# Revit family: 30501
name_source: partatom
category: Lighting Fixtures
revit_build: Autodesk Revit 2018 (Build: 20170223_1515(x64)
units: mm (PartAtom-declared; Revit-internal decimal feet)

## family parameters
Cut with Voids When Loaded = No
Host = Face
Light Source = Yes
OmniClass Number = 23.80.70.00
OmniClass Title = Lighting
Part Type = Normal
Room Calculation Point = No
Round Connector Dimension = Use Diameter
Shared = No

## types (1)
- 0030501 INSAVER SLIM UGR19 IP44 150 1200LM 840
    Apparent Load = 10 VA
    Assembly Code = D5020200
    AssetType = Fixed
    ClassificationName = Uniclass2015
    ClassificationValue = EF_70_80
    Color Filter = 16777215
    Cost = 0 $
    Default Elevation = 1219 mm
    Description = Insaver Slim is a ceiling recessed LED downlight (IP44 from the front),Die-cast aluminium body, loop in loop out connector for quick installation, Non dimmable LED driver, 9.5W; 1200lm; 126lm/W; 4000K; UGR <19 with shallow product depth 50mm. Meets TP(a) requirements.
    DiameterRecess_SYL = 150 mm
    DiameterTopBase_SYL = 150 mm
    DiameterTop_SYL = 98 mm  [stored 0.321522 ft]
    Diameter_SYL = 165 mm
    Dimming Lamp Color Temperature Shift = <None>
    DocumentationLiterature = http://www.sylvania-lighting.com
    DurationUnit = hours
    ElectricShockClassification = 126
    Emit Shape Visible in Rendering = No
    Emit from Circle Diameter = 125 mm  [stored 0.410105 ft]
    ExpectedLife = 50000
    HeightBezel_SYL = 3 mm  [stored 0.00984252 ft]
    Height_SYL = 61 mm  [stored 0.200131 ft]
    IfcExportAs = Class II
    IfcExportType = IfcLightFixtureType
    ImpactProtectionIndex = IfcLightFixtureType
    IngressProtection = IfcLightFixtureType
    InputNominalFrequency = 4000
    InputVoltage = 0
    LampColourRenderingIndex = 16500
    LampColourTemperature = LED
    LampMacAdamStep = 80
    LampNominalLuminous = 4000 K
    LightOutputRatio = LED
    LuminaireType = 0
    ManufacturerName = 126 lm/W
    Material = Feilo Sylvania
    Material_1_FEILO = Trim-Sylvania-STARTDownlight-White
    Material_2_FEILO = Diffuser-Sylvania-STARTDownlight
    Material_3_FEILO = Top-Sylvania-STARTDownlight
    Material_4_FEILO = LED-Sylvania-STARTDownlight
    Model = Insaver Slim UGR19 IP44 150 1200lm 840
    ModelNumber = 0030501
    ModelReference = Insaver Slim UGR19 IP44 150 1200lm 840
    Name = Insaver Slim UGR19 IP44 150 1200lm 840
    NominalDepth = 165 mm
    NominalHeight = 50 mm  [stored 0.164042 ft]
    NominalLength = 165 mm
    Photometric Web File = 0030501.IES
    PowerConsumption = Lighting
    PowerFactor = 0.9
    RadiusReflector_SYL = 85 mm  [stored 0.278871 ft]
    RadiusTop_SYL = 6 mm  [stored 0.019685 ft]
    Size1_SYL = Yes
    Size2_SYL = No
    Size3PIR_SYL = No
    Size4_SYL = No
    Tilt Angle = -90.00°
    Type Image = <None>
    TypeName = Insaver Slim UGR19 IP44 150 1200lm 840
    URL = 0.9
    VisibilityPIR_SYL = No
    Voltage = 230 V
    WarrantyDescription = http://www.sylvania-lighting.com
    WidthBezel_SYL = 20 mm  [stored 0.0656168 ft]

note: [stored X ft] marks values corroborated as IEEE doubles in the binary element streams (Revit-internal decimal feet)

## geometry (parser evidence)
native form markers: Sweep x2
no freeform markers — native parametric forms only
